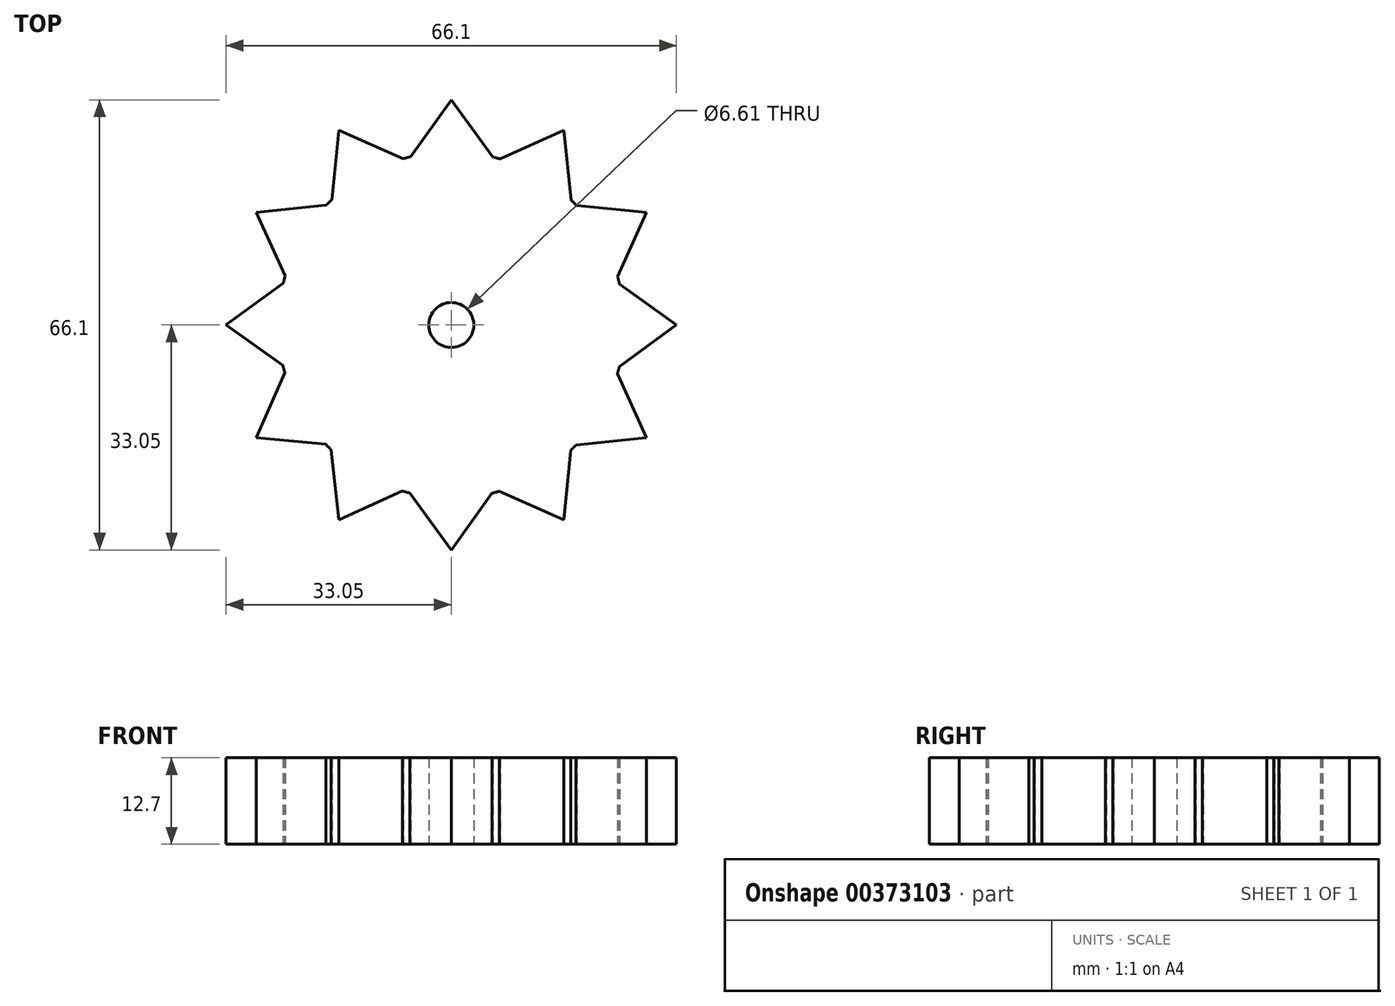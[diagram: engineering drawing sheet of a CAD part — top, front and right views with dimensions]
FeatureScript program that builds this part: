
annotation { "Feature Type Name" : "Feature", "Feature Type Description" : "" }
export const myFeature = defineFeature(function(context is Context, id is Id, definition is map)
    precondition{}
    {
        {
            var Q0;
            Q0=qCreatedBy(makeId("Top.planeOp"),FACE);
            var sketch = newSketch(context, id + "F0", { "sketchPlane" : qUnion([Q0])});
            skCircle(sketch, "E0", {"center": v(0, 0) * mm, "radius": 3.3 * mm});
            skCircle(sketch, "E1", {"center": v(0, 0) * mm, "radius": 25.42 * mm});
            skLineSegment(sketch, "E2", {"start": v(0, 25.42) * mm, "end": v(0, 33.05) * mm});
            skLineSegment(sketch, "E3", {"start": v(0, 33.05) * mm, "end": v(6.1, 24.68) * mm});
            skLineSegment(sketch, "E4", {"start": v(0, 33.05) * mm, "end": v(-5.97, 24.7) * mm});
            skLineSegment(sketch, "E5.1.0", {"start": v(-16.52, 28.62) * mm, "end": v(-17.53, 18.41) * mm});
            skLineSegment(sketch, "E5.1.1", {"start": v(-16.52, 28.62) * mm, "end": v(-7.05, 24.42) * mm});
            skLineSegment(sketch, "E5.2.0", {"start": v(-28.62, 16.52) * mm, "end": v(-24.39, 7.18) * mm});
            skLineSegment(sketch, "E5.2.1", {"start": v(-28.62, 16.52) * mm, "end": v(-18.32, 17.62) * mm});
            skLineSegment(sketch, "E5.3.0", {"start": v(-33.05, 0) * mm, "end": v(-24.7, -5.97) * mm});
            skLineSegment(sketch, "E5.3.1", {"start": v(-33.05, 0) * mm, "end": v(-24.68, 6.1) * mm});
            skLineSegment(sketch, "E5.4.0", {"start": v(-28.62, -16.52) * mm, "end": v(-18.41, -17.53) * mm});
            skLineSegment(sketch, "E5.4.1", {"start": v(-28.62, -16.52) * mm, "end": v(-24.42, -7.05) * mm});
            skLineSegment(sketch, "E5.5.0", {"start": v(-16.52, -28.62) * mm, "end": v(-7.18, -24.39) * mm});
            skLineSegment(sketch, "E5.5.1", {"start": v(-16.52, -28.62) * mm, "end": v(-17.62, -18.32) * mm});
            skLineSegment(sketch, "E5.6.0", {"start": v(0, -33.05) * mm, "end": v(5.97, -24.7) * mm});
            skLineSegment(sketch, "E5.6.1", {"start": v(0, -33.05) * mm, "end": v(-6.1, -24.68) * mm});
            skLineSegment(sketch, "E5.7.0", {"start": v(16.52, -28.62) * mm, "end": v(17.53, -18.41) * mm});
            skLineSegment(sketch, "E5.7.1", {"start": v(16.52, -28.62) * mm, "end": v(7.05, -24.42) * mm});
            skLineSegment(sketch, "E5.8.0", {"start": v(28.62, -16.52) * mm, "end": v(24.39, -7.18) * mm});
            skLineSegment(sketch, "E5.8.1", {"start": v(28.62, -16.52) * mm, "end": v(18.32, -17.62) * mm});
            skLineSegment(sketch, "E5.9.0", {"start": v(33.05, 0) * mm, "end": v(24.7, 5.97) * mm});
            skLineSegment(sketch, "E5.9.1", {"start": v(33.05, 0) * mm, "end": v(24.68, -6.1) * mm});
            skLineSegment(sketch, "E5.10.0", {"start": v(28.62, 16.52) * mm, "end": v(18.41, 17.53) * mm});
            skLineSegment(sketch, "E5.10.1", {"start": v(28.62, 16.52) * mm, "end": v(24.42, 7.05) * mm});
            skLineSegment(sketch, "E5.11.0", {"start": v(16.52, 28.62) * mm, "end": v(7.18, 24.39) * mm});
            skLineSegment(sketch, "E5.11.1", {"start": v(16.52, 28.62) * mm, "end": v(17.62, 18.32) * mm});
            skSolve(sketch);
        }
        {
            var Q0;
            Q0 = qSketchRegion(id + "F0", true);
            extrude(context, id + "F1", {"entities" : qUnion([Q0]), "depth" : 12.7 * mm});
        }
    });
